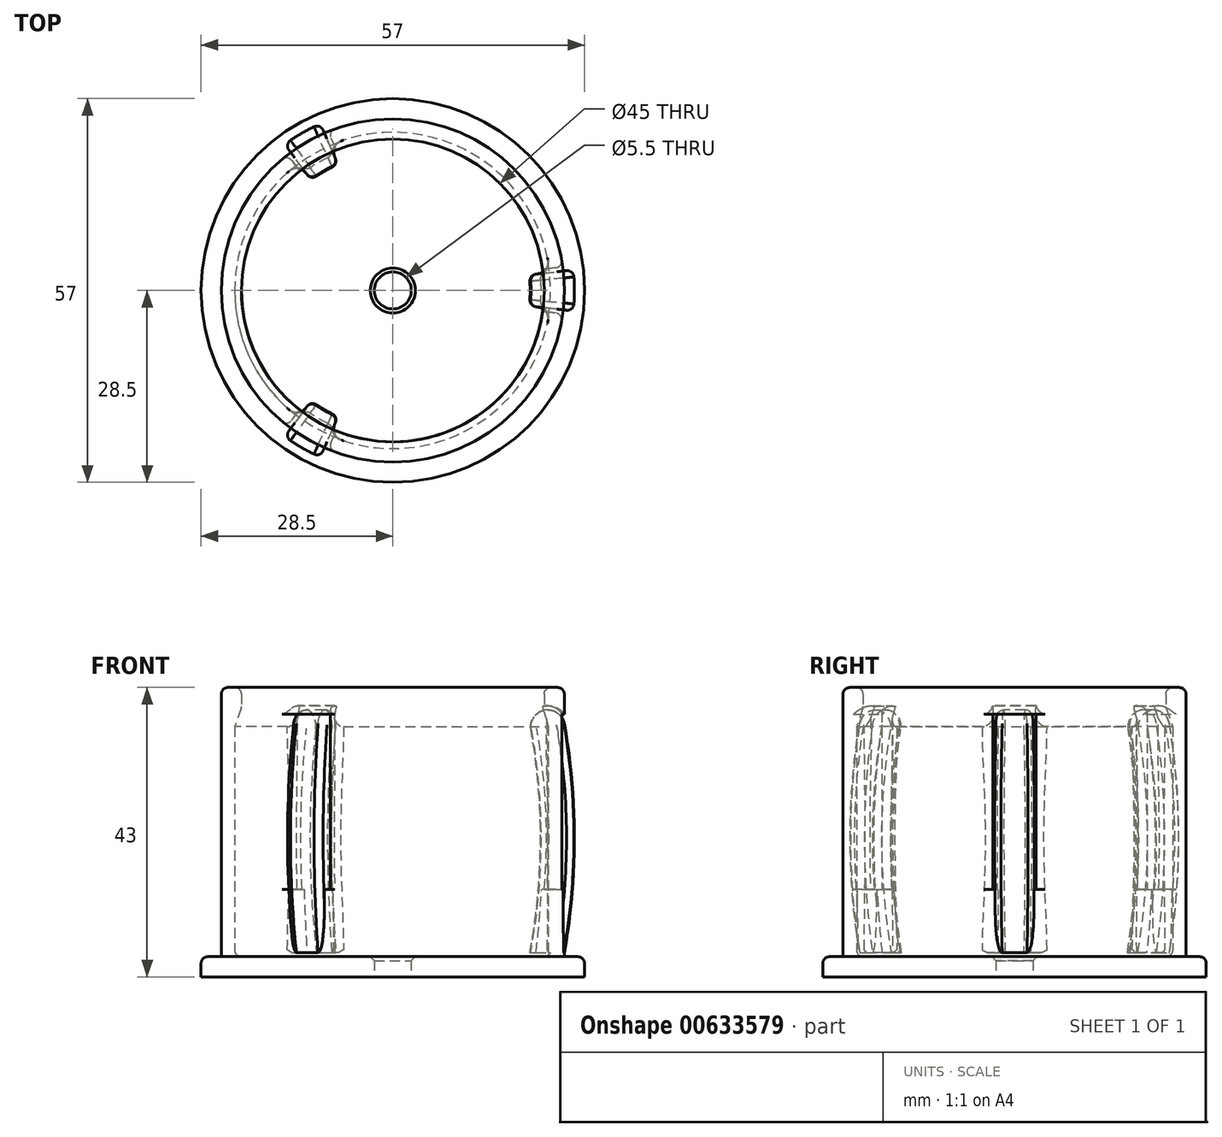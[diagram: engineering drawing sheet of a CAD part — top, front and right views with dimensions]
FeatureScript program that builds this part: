
annotation { "Feature Type Name" : "Feature", "Feature Type Description" : "" }
export const myFeature = defineFeature(function(context is Context, id is Id, definition is map)
    precondition{}
    {
        {
            var Q0;
            Q0=qCreatedBy(makeId("Front.planeOp"),FACE);
            var sketch = newSketch(context, id + "F0", { "sketchPlane" : qUnion([Q0])});
            skLineSegment(sketch, "E0", {"start": v(2.75, -1.5) * mm, "end": v(2.75, 1.5) * mm});
            skLineSegment(sketch, "E1", {"start": v(2.75, 1.5) * mm, "end": v(23.5, 1.5) * mm});
            skLineSegment(sketch, "E2", {"start": v(25.5, 1.5) * mm, "end": v(25.5, 41.5) * mm});
            skLineSegment(sketch, "E3", {"start": v(22.5, 41.5) * mm, "end": v(25.5, 41.5) * mm});
            skLineSegment(sketch, "E4", {"start": v(23.5, 35.67) * mm, "end": v(23.5, 1.5) * mm});
            skLineSegment(sketch, "E5", {"start": v(25.5, 1.5) * mm, "end": v(28.5, 1.5) * mm});
            skLineSegment(sketch, "E6", {"start": v(28.5, 1.5) * mm, "end": v(28.5, -1.5) * mm});
            skLineSegment(sketch, "E7", {"start": v(28.5, -1.5) * mm, "end": v(2.75, -1.5) * mm});
            skLineSegment(sketch, "E8", {"start": v(0, -12.71) * mm, "end": v(0, 50.95) * mm, "construction": true});
            skPoint(sketch, "E9.visualSharp", {"position": v(23.5, 1.5) * mm});
            skLineSegment(sketch, "E10", {"start": v(22.5, 41.5) * mm, "end": v(22.5, 38.5) * mm});
            skLineSegment(sketch, "E11", {"start": v(22.5, 38.5) * mm, "end": v(23.5, 35.67) * mm});
            skLineSegment(sketch, "E12", {"start": v(24.5, 1.5) * mm, "end": v(24.5, 41.5) * mm, "construction": true});
            skSolve(sketch);
        }
        {
            var Q0;
            Q0=qSketchRegion(id+"F0",true);
            var Q1;
            Q1=sQuery(id+"F0.wireOp",EDGE,"E8");
            revolve(context, id + "F1", {"entities" : qUnion([Q0]), "axis" : qUnion([Q1]), "revolveType" : RevolveType.FULL});
        }
        {
            var Q0;
            Q0=qCreatedBy(makeId("Front.planeOp"),FACE);
            var sketch = newSketch(context, id + "F2", { "sketchPlane" : qUnion([Q0])});
            skLineSegment(sketch, "E13", {"start": v(27, 29.31) * mm, "end": v(27, 4.9) * mm, "construction": true});
            skArc(sketch, "E14", {"start": v(25.5, 36.1) * mm, "mid": v(27, 19.1) * mm, "end": v(25.5, 2.1) * mm});
            skArc(sketch, "E15", {"start": v(20.58, 35.23) * mm, "mid": v(22, 18.66) * mm, "end": v(20.42, 2.1) * mm});
            skLineSegment(sketch, "E16", {"start": v(20.42, 2.1) * mm, "end": v(25.5, 2.1) * mm});
            skArc(sketch, "E17", {"start": v(20.58, 35.23) * mm, "mid": v(22.6, 38.13) * mm, "end": v(25.5, 36.1) * mm});
            skLineSegment(sketch, "E18", {"start": v(21.36, 35.67) * mm, "end": v(26.51, 35.67) * mm, "construction": true});
            skSolve(sketch);
        }
        {
            var Q0;
            Q0=qSketchRegion(id+"F2",true);
            var Q1;
            Q1=sQuery(id+"F0.wireOp",EDGE,"E8");
            revolve(context, id + "F3", {"entities" : qUnion([Q0]), "axis" : qUnion([Q1]), "revolveType" : RevolveType.SYMMETRIC, "angle" : 13 * degree});
        }
        {
            var Q0;
            Q0=makeQuery(id+"F3.opRevolve","SWEPT_BODY",BODY,{"disambiguationData":[OSD([sQuery(id+"F2.wireOp",EDGE,"E14"),sQuery(id+"F2.wireOp",EDGE,"E15"),sQuery(id+"F2.wireOp",EDGE,"ehrXcVqz-ctuI-yXWO-wcDy-QBcCehmGWMRg"),sQuery(id+"F2.wireOp",EDGE,"7emjYWeK-92yS-v46Q-MAfY-u0VWEbS8i3fu")])]});
            var Q1;
            Q1=sQuery(id+"F0.wireOp",EDGE,"E8");
            circularPattern(context, id + "F4", {"entities" : qUnion([Q0]), "axis" : qUnion([Q1]), "angle" : 360 * degree, "instanceCount" : 3, "equalSpace" : true});
        }
        {
            var Q0;
            Q0=makeQuery(id+"F3.opRevolve","SWEPT_BODY",BODY,{"disambiguationData":[OSD([sQuery(id+"F2.wireOp",EDGE,"E14"),sQuery(id+"F2.wireOp",EDGE,"E15"),sQuery(id+"F2.wireOp",EDGE,"ehrXcVqz-ctuI-yXWO-wcDy-QBcCehmGWMRg"),sQuery(id+"F2.wireOp",EDGE,"7emjYWeK-92yS-v46Q-MAfY-u0VWEbS8i3fu")])]});
            var Q1;
            Q1=makeQuery(id+"F4.opPattern","COPY",BODY,{"derivedFrom":makeQuery(id+"F3.opRevolve","SWEPT_BODY",BODY,{"disambiguationData":[OSD([sQuery(id+"F2.wireOp",EDGE,"E14"),sQuery(id+"F2.wireOp",EDGE,"E15"),sQuery(id+"F2.wireOp",EDGE,"ehrXcVqz-ctuI-yXWO-wcDy-QBcCehmGWMRg"),sQuery(id+"F2.wireOp",EDGE,"7emjYWeK-92yS-v46Q-MAfY-u0VWEbS8i3fu")])]}),"instanceName":"2"});
            var Q2;
            Q2=makeQuery(id+"F4.opPattern","COPY",BODY,{"derivedFrom":makeQuery(id+"F3.opRevolve","SWEPT_BODY",BODY,{"disambiguationData":[OSD([sQuery(id+"F2.wireOp",EDGE,"E14"),sQuery(id+"F2.wireOp",EDGE,"E15"),sQuery(id+"F2.wireOp",EDGE,"ehrXcVqz-ctuI-yXWO-wcDy-QBcCehmGWMRg"),sQuery(id+"F2.wireOp",EDGE,"7emjYWeK-92yS-v46Q-MAfY-u0VWEbS8i3fu")])]}),"instanceName":"1"});
            var Q3;
            Q3=makeQuery(id+"F1.opRevolve","SWEPT_BODY",BODY,{"disambiguationData":[OSD([sQuery(id+"F0.wireOp",EDGE,"E0"),sQuery(id+"F0.wireOp",EDGE,"E1"),sQuery(id+"F0.wireOp",EDGE,"E2"),sQuery(id+"F0.wireOp",EDGE,"E3"),sQuery(id+"F0.wireOp",EDGE,"E4"),sQuery(id+"F0.wireOp",EDGE,"E5"),sQuery(id+"F0.wireOp",EDGE,"E6"),sQuery(id+"F0.wireOp",EDGE,"E7")])]});
            booleanBodies(context, id + "F5", {"operationType" : BooleanOperationType.SUBTRACTION, "tools" : qUnion([Q0, Q1, Q2]), "targets" : qUnion([Q3]), "offset" : true, "offsetAll" : true, "offsetDistance" : 0.6 * mm, "reFillet" : true, "keepTools" : true});
        }
        {
            var Q0;
            Q0=makeQuery(id+"F1.opRevolve","SWEPT_FACE",FACE,{"disambiguationData":[OSD([sQuery(id+"F0.wireOp",EDGE,"E1")])]});
            var sketch = newSketch(context, id + "F6", { "sketchPlane" : qUnion([Q0])});
            skCircle(sketch, "E19", {"center": v(0, 0) * mm, "radius": 23.5 * mm});
            skCircle(sketch, "E20", {"center": v(0, 0) * mm, "radius": 25.5 * mm});
            skSolve(sketch);
        }
        {
            var Q0;
            Q0=qSketchRegion(id+"F6",true);
            extrude(context, id + "F7", {"entities" : qUnion([Q0]), "depth" : 10 * mm});
        }
        {
            var Q0;
            Q0=makeQuery(id+"F1.opRevolve","SWEPT_BODY",BODY,{"disambiguationData":[OSD([sQuery(id+"F0.wireOp",EDGE,"E0"),sQuery(id+"F0.wireOp",EDGE,"E1"),sQuery(id+"F0.wireOp",EDGE,"E2"),sQuery(id+"F0.wireOp",EDGE,"E3"),sQuery(id+"F0.wireOp",EDGE,"E4"),sQuery(id+"F0.wireOp",EDGE,"E5"),sQuery(id+"F0.wireOp",EDGE,"E6"),sQuery(id+"F0.wireOp",EDGE,"E7")])]});
            var Q1;
            Q1=makeQuery(id+"FhO7E1VeGoCWiRw_1.opExtrude","SWEPT_BODY",BODY,{"disambiguationData":[OSD([sQuery(id+"F2.wireOp",EDGE,"E14"),sQuery(id+"F2.wireOp",EDGE,"E15"),sQuery(id+"F2.wireOp",EDGE,"ehrXcVqz-ctuI-yXWO-wcDy-QBcCehmGWMRg"),sQuery(id+"F2.wireOp",EDGE,"7emjYWeK-92yS-v46Q-MAfY-u0VWEbS8i3fu")])]});
            var Q2;
            Q2=makeQuery(id+"F4.opPattern","COPY",BODY,{"derivedFrom":makeQuery(id+"FhO7E1VeGoCWiRw_1.opExtrude","SWEPT_BODY",BODY,{"disambiguationData":[OSD([sQuery(id+"F2.wireOp",EDGE,"E14"),sQuery(id+"F2.wireOp",EDGE,"E15"),sQuery(id+"F2.wireOp",EDGE,"ehrXcVqz-ctuI-yXWO-wcDy-QBcCehmGWMRg"),sQuery(id+"F2.wireOp",EDGE,"7emjYWeK-92yS-v46Q-MAfY-u0VWEbS8i3fu")])]}),"instanceName":"1"});
            var Q3;
            Q3=makeQuery(id+"F4.opPattern","COPY",BODY,{"derivedFrom":makeQuery(id+"FhO7E1VeGoCWiRw_1.opExtrude","SWEPT_BODY",BODY,{"disambiguationData":[OSD([sQuery(id+"F2.wireOp",EDGE,"E14"),sQuery(id+"F2.wireOp",EDGE,"E15"),sQuery(id+"F2.wireOp",EDGE,"ehrXcVqz-ctuI-yXWO-wcDy-QBcCehmGWMRg"),sQuery(id+"F2.wireOp",EDGE,"7emjYWeK-92yS-v46Q-MAfY-u0VWEbS8i3fu")])]}),"instanceName":"2"});
            var Q4;
            Q4=makeQuery(id+"F7.opExtrude","SWEPT_BODY",BODY,{"disambiguationData":[OSD([sQuery(id+"F6.wireOp",EDGE,"E19"),sQuery(id+"F6.wireOp",EDGE,"E20")])]});
            booleanBodies(context, id + "F8", {"operationType" : BooleanOperationType.UNION, "tools" : qUnion([Q0, Q1, Q2, Q3, Q4])});
        }
        {
            var Q0;
            Q0=makeQuery(id+"F1.opRevolve","SWEPT_BODY",BODY,{"disambiguationData":[OSD([sQuery(id+"F0.wireOp",EDGE,"E0"),sQuery(id+"F0.wireOp",EDGE,"E1"),sQuery(id+"F0.wireOp",EDGE,"E2"),sQuery(id+"F0.wireOp",EDGE,"E3"),sQuery(id+"F0.wireOp",EDGE,"E4"),sQuery(id+"F0.wireOp",EDGE,"E5"),sQuery(id+"F0.wireOp",EDGE,"E6"),sQuery(id+"F0.wireOp",EDGE,"E7")])]});
            var Q1;
            Q1=makeQuery(id+"F3.opRevolve","SWEPT_BODY",BODY,{"disambiguationData":[OSD([sQuery(id+"F2.wireOp",EDGE,"E14"),sQuery(id+"F2.wireOp",EDGE,"E15"),sQuery(id+"F2.wireOp",EDGE,"ehrXcVqz-ctuI-yXWO-wcDy-QBcCehmGWMRg"),sQuery(id+"F2.wireOp",EDGE,"7emjYWeK-92yS-v46Q-MAfY-u0VWEbS8i3fu")])]});
            var Q2;
            Q2=makeQuery(id+"F4.opPattern","COPY",BODY,{"derivedFrom":makeQuery(id+"F3.opRevolve","SWEPT_BODY",BODY,{"disambiguationData":[OSD([sQuery(id+"F2.wireOp",EDGE,"E14"),sQuery(id+"F2.wireOp",EDGE,"E15"),sQuery(id+"F2.wireOp",EDGE,"ehrXcVqz-ctuI-yXWO-wcDy-QBcCehmGWMRg"),sQuery(id+"F2.wireOp",EDGE,"7emjYWeK-92yS-v46Q-MAfY-u0VWEbS8i3fu")])]}),"instanceName":"1"});
            var Q3;
            Q3=makeQuery(id+"F4.opPattern","COPY",BODY,{"derivedFrom":makeQuery(id+"F3.opRevolve","SWEPT_BODY",BODY,{"disambiguationData":[OSD([sQuery(id+"F2.wireOp",EDGE,"E14"),sQuery(id+"F2.wireOp",EDGE,"E15"),sQuery(id+"F2.wireOp",EDGE,"ehrXcVqz-ctuI-yXWO-wcDy-QBcCehmGWMRg"),sQuery(id+"F2.wireOp",EDGE,"7emjYWeK-92yS-v46Q-MAfY-u0VWEbS8i3fu")])]}),"instanceName":"2"});
            booleanBodies(context, id + "F9", {"operationType" : BooleanOperationType.UNION, "tools" : qUnion([Q0, Q1, Q2, Q3])});
        }
        {
            var Q0;
            Q0=makeQuery(id+"F4.opPattern","COPY",EDGE,{"derivedFrom":makeQuery(id+"F3.opRevolve","CAP_EDGE",EDGE,{"disambiguationData":[OSD([sQuery(id+"F2.wireOp",EDGE,"E14")])],"isStart":false}),"instanceName":"1"});
            var Q1;
            Q1=makeQuery(id+"F4.opPattern","COPY",EDGE,{"derivedFrom":makeQuery(id+"F3.opRevolve","CAP_EDGE",EDGE,{"disambiguationData":[OSD([sQuery(id+"F2.wireOp",EDGE,"E14")])],"isStart":true}),"instanceName":"1"});
            var Q2;
            Q2=makeQuery(id+"F4.opPattern","COPY",EDGE,{"derivedFrom":makeQuery(id+"F3.opRevolve","CAP_EDGE",EDGE,{"disambiguationData":[OSD([sQuery(id+"F2.wireOp",EDGE,"E14")])],"isStart":true}),"instanceName":"2"});
            var Q3;
            Q3=makeQuery(id+"F4.opPattern","COPY",EDGE,{"derivedFrom":makeQuery(id+"F3.opRevolve","CAP_EDGE",EDGE,{"disambiguationData":[OSD([sQuery(id+"F2.wireOp",EDGE,"E14")])],"isStart":false}),"instanceName":"2"});
            var Q4;
            Q4=makeQuery(id+"F3.opRevolve","CAP_EDGE",EDGE,{"disambiguationData":[OSD([sQuery(id+"F2.wireOp",EDGE,"E14")])],"isStart":true});
            var Q5;
            Q5=makeQuery(id+"F3.opRevolve","CAP_EDGE",EDGE,{"disambiguationData":[OSD([sQuery(id+"F2.wireOp",EDGE,"E14")])],"isStart":false});
            var Q6;
            Q6=makeQuery(id+"F5.tempBoolean.opBoolean","INTERSECT",EDGE,{"derivedFrom":[makeQuery(id+"F1.opRevolve","SWEPT_FACE",FACE,{"disambiguationData":[OSD([sQuery(id+"F0.wireOp",EDGE,"E2")])]}),makeQuery(id+"F5.offsetTempBody.opPattern","COPY",FACE,{"derivedFrom":makeQuery(id+"F4.opPattern","COPY",FACE,{"derivedFrom":makeQuery(id+"F3.opRevolve","CAP_FACE",FACE,{"disambiguationData":[OSD([sQuery(id+"F2.wireOp",EDGE,"E14"),sQuery(id+"F2.wireOp",EDGE,"E15"),sQuery(id+"F2.wireOp",EDGE,"ehrXcVqz-ctuI-yXWO-wcDy-QBcCehmGWMRg"),sQuery(id+"F2.wireOp",EDGE,"7emjYWeK-92yS-v46Q-MAfY-u0VWEbS8i3fu")])],"isStart":false}),"instanceName":"1"}),"instanceName":"1"})]});
            var Q7;
            Q7=makeQuery(id+"F5.tempBoolean.opBoolean","INTERSECT",EDGE,{"derivedFrom":[makeQuery(id+"F1.opRevolve","SWEPT_FACE",FACE,{"disambiguationData":[OSD([sQuery(id+"F0.wireOp",EDGE,"E2")])]}),makeQuery(id+"F5.offsetTempBody.opPattern","COPY",FACE,{"derivedFrom":makeQuery(id+"F4.opPattern","COPY",FACE,{"derivedFrom":makeQuery(id+"F3.opRevolve","CAP_FACE",FACE,{"disambiguationData":[OSD([sQuery(id+"F2.wireOp",EDGE,"E14"),sQuery(id+"F2.wireOp",EDGE,"E15"),sQuery(id+"F2.wireOp",EDGE,"ehrXcVqz-ctuI-yXWO-wcDy-QBcCehmGWMRg"),sQuery(id+"F2.wireOp",EDGE,"7emjYWeK-92yS-v46Q-MAfY-u0VWEbS8i3fu")])],"isStart":true}),"instanceName":"1"}),"instanceName":"1"})]});
            var Q8;
            Q8=makeQuery(id+"F5.tempBoolean.opBoolean","INTERSECT",EDGE,{"derivedFrom":[makeQuery(id+"F1.opRevolve","SWEPT_FACE",FACE,{"disambiguationData":[OSD([sQuery(id+"F0.wireOp",EDGE,"E2")])]}),makeQuery(id+"F5.offsetTempBody.opPattern","COPY",FACE,{"derivedFrom":makeQuery(id+"F3.opRevolve","CAP_FACE",FACE,{"disambiguationData":[OSD([sQuery(id+"F2.wireOp",EDGE,"E14"),sQuery(id+"F2.wireOp",EDGE,"E15"),sQuery(id+"F2.wireOp",EDGE,"ehrXcVqz-ctuI-yXWO-wcDy-QBcCehmGWMRg"),sQuery(id+"F2.wireOp",EDGE,"7emjYWeK-92yS-v46Q-MAfY-u0VWEbS8i3fu")])],"isStart":false}),"instanceName":"1"})]});
            var Q9;
            Q9=makeQuery(id+"F5.tempBoolean.opBoolean","INTERSECT",EDGE,{"derivedFrom":[makeQuery(id+"F1.opRevolve","SWEPT_FACE",FACE,{"disambiguationData":[OSD([sQuery(id+"F0.wireOp",EDGE,"E2")])]}),makeQuery(id+"F5.offsetTempBody.opPattern","COPY",FACE,{"derivedFrom":makeQuery(id+"F3.opRevolve","CAP_FACE",FACE,{"disambiguationData":[OSD([sQuery(id+"F2.wireOp",EDGE,"E14"),sQuery(id+"F2.wireOp",EDGE,"E15"),sQuery(id+"F2.wireOp",EDGE,"ehrXcVqz-ctuI-yXWO-wcDy-QBcCehmGWMRg"),sQuery(id+"F2.wireOp",EDGE,"7emjYWeK-92yS-v46Q-MAfY-u0VWEbS8i3fu")])],"isStart":true}),"instanceName":"1"})]});
            var Q10;
            Q10=makeQuery(id+"F5.tempBoolean.opBoolean","INTERSECT",EDGE,{"derivedFrom":[makeQuery(id+"F1.opRevolve","SWEPT_FACE",FACE,{"disambiguationData":[OSD([sQuery(id+"F0.wireOp",EDGE,"E2")])]}),makeQuery(id+"F5.offsetTempBody.opPattern","COPY",FACE,{"derivedFrom":makeQuery(id+"F4.opPattern","COPY",FACE,{"derivedFrom":makeQuery(id+"F3.opRevolve","CAP_FACE",FACE,{"disambiguationData":[OSD([sQuery(id+"F2.wireOp",EDGE,"E14"),sQuery(id+"F2.wireOp",EDGE,"E15"),sQuery(id+"F2.wireOp",EDGE,"ehrXcVqz-ctuI-yXWO-wcDy-QBcCehmGWMRg"),sQuery(id+"F2.wireOp",EDGE,"7emjYWeK-92yS-v46Q-MAfY-u0VWEbS8i3fu")])],"isStart":false}),"instanceName":"2"}),"instanceName":"1"})]});
            var Q11;
            Q11=makeQuery(id+"F5.tempBoolean.opBoolean","INTERSECT",EDGE,{"derivedFrom":[makeQuery(id+"F1.opRevolve","SWEPT_FACE",FACE,{"disambiguationData":[OSD([sQuery(id+"F0.wireOp",EDGE,"E2")])]}),makeQuery(id+"F5.offsetTempBody.opPattern","COPY",FACE,{"derivedFrom":makeQuery(id+"F4.opPattern","COPY",FACE,{"derivedFrom":makeQuery(id+"F3.opRevolve","CAP_FACE",FACE,{"disambiguationData":[OSD([sQuery(id+"F2.wireOp",EDGE,"E14"),sQuery(id+"F2.wireOp",EDGE,"E15"),sQuery(id+"F2.wireOp",EDGE,"ehrXcVqz-ctuI-yXWO-wcDy-QBcCehmGWMRg"),sQuery(id+"F2.wireOp",EDGE,"7emjYWeK-92yS-v46Q-MAfY-u0VWEbS8i3fu")])],"isStart":true}),"instanceName":"2"}),"instanceName":"1"})]});
            var Q12;
            Q12=makeQuery(id+"F1.opRevolve","SWEPT_EDGE",EDGE,{"disambiguationData":[OSD([sQuery(id+"F0.wireOp",EDGE,"E5"),sQuery(id+"F0.wireOp",EDGE,"E6")])]});
            var Q13;
            Q13=makeQuery(id+"F1.opRevolve","SWEPT_EDGE",EDGE,{"disambiguationData":[OSD([sQuery(id+"F0.wireOp",EDGE,"E1"),sQuery(id+"F0.wireOp",EDGE,"E4")])]});
            var Q14;
            Q14=makeQuery(id+"F1.opRevolve","SWEPT_EDGE",EDGE,{"disambiguationData":[OSD([sQuery(id+"F0.wireOp",EDGE,"E2"),sQuery(id+"F0.wireOp",EDGE,"E3")])]});
            var Q15;
            Q15=makeQuery(id+"F1.opRevolve","SWEPT_EDGE",EDGE,{"disambiguationData":[OSD([sQuery(id+"F0.wireOp",EDGE,"E3"),sQuery(id+"F0.wireOp",EDGE,"E10")])]});
            var Q16;
            Q16=makeQuery(id+"F1.opRevolve","SWEPT_EDGE",EDGE,{"disambiguationData":[OSD([sQuery(id+"F0.wireOp",EDGE,"E10"),sQuery(id+"F0.wireOp",EDGE,"44e6730c-d766-4bbe-a9cf-efe5463532ff")])]});
            fillet(context, id + "F10", {"entities" : qUnion([Q0, Q1, Q2, Q3, Q4, Q5, Q6, Q7, Q8, Q9, Q10, Q11, Q12, Q13, Q14, Q15, Q16]), "radius" : 1 * mm, "tangentPropagation" : true, "allowEdgeOverflow" : false});
        }
        {
            var Q0;
            {var subQ2=sQuery(id+"F2.wireOp",EDGE,"E17");var subQ3=sQuery(id+"F2.wireOp",EDGE,"E16");var subQ4=sQuery(id+"F2.wireOp",EDGE,"E15");var subQ5=sQuery(id+"F2.wireOp",EDGE,"E14");var subQ6=makeQuery(id+"F3.opRevolve","CAP_FACE",FACE,{"disambiguationData":[OSD([subQ5,subQ4,subQ3,subQ2])],"isStart":false});var subQ7=makeQuery(id+"F3.opRevolve","CAP_FACE",FACE,{"disambiguationData":[OSD([subQ5,subQ4,subQ3,subQ2])],"isStart":true});var subQ8=makeQuery(id+"F1.opRevolve","SWEPT_FACE",FACE,{"disambiguationData":[OSD([sQuery(id+"F0.wireOp",EDGE,"E4")])]});Q0=makeQuery(id+"F9.opBoolean","INTERSECT",EDGE,{"derivedFrom":[subQ7,makeQuery(id+"F8.opBoolean","MERGE",FACE,{"derivedFrom":[makeQuery(id+"F5.tempBoolean.opBoolean","SPLIT",FACE,{"disambiguationData":[TD([makeQuery(id+"F5.offsetTempBody.opPattern","COPY",FACE,{"derivedFrom":subQ7,"instanceName":"1"})])],"derivedFrom":subQ8}),makeQuery(id+"F5.tempBoolean.opBoolean","SPLIT",FACE,{"disambiguationData":[TD([makeQuery(id+"F5.offsetTempBody.opPattern","COPY",FACE,{"derivedFrom":subQ6,"instanceName":"1"})])],"derivedFrom":subQ8}),makeQuery(id+"F5.tempBoolean.opBoolean","SPLIT",FACE,{"disambiguationData":[TD([makeQuery(id+"F5.offsetTempBody.opPattern","COPY",FACE,{"derivedFrom":makeQuery(id+"F4.opPattern","COPY",FACE,{"derivedFrom":subQ6,"instanceName":"1"}),"instanceName":"1"})])],"derivedFrom":subQ8}),makeQuery(id+"F7.opExtrude","SWEPT_FACE",FACE,{"disambiguationData":[OSD([sQuery(id+"F6.wireOp",EDGE,"E19")])]})]})]});}
            var Q1;
            {var subQ2=sQuery(id+"F2.wireOp",EDGE,"E17");var subQ3=sQuery(id+"F2.wireOp",EDGE,"E16");var subQ4=sQuery(id+"F2.wireOp",EDGE,"E15");var subQ5=sQuery(id+"F2.wireOp",EDGE,"E14");var subQ6=makeQuery(id+"F3.opRevolve","CAP_FACE",FACE,{"disambiguationData":[OSD([subQ5,subQ4,subQ3,subQ2])],"isStart":false});var subQ7=makeQuery(id+"F3.opRevolve","CAP_FACE",FACE,{"disambiguationData":[OSD([subQ5,subQ4,subQ3,subQ2])],"isStart":true});var subQ8=makeQuery(id+"F1.opRevolve","SWEPT_FACE",FACE,{"disambiguationData":[OSD([sQuery(id+"F0.wireOp",EDGE,"E4")])]});Q1=makeQuery(id+"F9.opBoolean","INTERSECT",EDGE,{"derivedFrom":[subQ6,makeQuery(id+"F8.opBoolean","MERGE",FACE,{"derivedFrom":[makeQuery(id+"F5.tempBoolean.opBoolean","SPLIT",FACE,{"disambiguationData":[TD([makeQuery(id+"F5.offsetTempBody.opPattern","COPY",FACE,{"derivedFrom":subQ7,"instanceName":"1"})])],"derivedFrom":subQ8}),makeQuery(id+"F5.tempBoolean.opBoolean","SPLIT",FACE,{"disambiguationData":[TD([makeQuery(id+"F5.offsetTempBody.opPattern","COPY",FACE,{"derivedFrom":subQ6,"instanceName":"1"})])],"derivedFrom":subQ8}),makeQuery(id+"F5.tempBoolean.opBoolean","SPLIT",FACE,{"disambiguationData":[TD([makeQuery(id+"F5.offsetTempBody.opPattern","COPY",FACE,{"derivedFrom":makeQuery(id+"F4.opPattern","COPY",FACE,{"derivedFrom":subQ6,"instanceName":"1"}),"instanceName":"1"})])],"derivedFrom":subQ8}),makeQuery(id+"F7.opExtrude","SWEPT_FACE",FACE,{"disambiguationData":[OSD([sQuery(id+"F6.wireOp",EDGE,"E19")])]})]})]});}
            var Q2;
            {var subQ2=sQuery(id+"F2.wireOp",EDGE,"E17");var subQ3=sQuery(id+"F2.wireOp",EDGE,"E16");var subQ4=sQuery(id+"F2.wireOp",EDGE,"E15");var subQ5=sQuery(id+"F2.wireOp",EDGE,"E14");var subQ6=makeQuery(id+"F3.opRevolve","CAP_FACE",FACE,{"disambiguationData":[OSD([subQ5,subQ4,subQ3,subQ2])],"isStart":false});var subQ7=makeQuery(id+"F3.opRevolve","CAP_FACE",FACE,{"disambiguationData":[OSD([subQ5,subQ4,subQ3,subQ2])],"isStart":true});var subQ8=makeQuery(id+"F1.opRevolve","SWEPT_FACE",FACE,{"disambiguationData":[OSD([sQuery(id+"F0.wireOp",EDGE,"E4")])]});var subQ9=makeQuery(id+"F4.opPattern","COPY",FACE,{"derivedFrom":subQ6,"instanceName":"2"});Q2=makeQuery(id+"F9.opBoolean","INTERSECT",EDGE,{"derivedFrom":[subQ9,makeQuery(id+"F8.opBoolean","MERGE",FACE,{"derivedFrom":[makeQuery(id+"F5.tempBoolean.opBoolean","SPLIT",FACE,{"disambiguationData":[TD([makeQuery(id+"F5.offsetTempBody.opPattern","COPY",FACE,{"derivedFrom":subQ7,"instanceName":"1"})])],"derivedFrom":subQ8}),makeQuery(id+"F5.tempBoolean.opBoolean","SPLIT",FACE,{"disambiguationData":[TD([makeQuery(id+"F5.offsetTempBody.opPattern","COPY",FACE,{"derivedFrom":subQ6,"instanceName":"1"})])],"derivedFrom":subQ8}),makeQuery(id+"F5.tempBoolean.opBoolean","SPLIT",FACE,{"disambiguationData":[TD([makeQuery(id+"F5.offsetTempBody.opPattern","COPY",FACE,{"derivedFrom":makeQuery(id+"F4.opPattern","COPY",FACE,{"derivedFrom":subQ6,"instanceName":"1"}),"instanceName":"1"})])],"derivedFrom":subQ8}),makeQuery(id+"F7.opExtrude","SWEPT_FACE",FACE,{"disambiguationData":[OSD([sQuery(id+"F6.wireOp",EDGE,"E19")])]})]})]});}
            var Q3;
            {var subQ2=sQuery(id+"F2.wireOp",EDGE,"E17");var subQ3=sQuery(id+"F2.wireOp",EDGE,"E16");var subQ4=sQuery(id+"F2.wireOp",EDGE,"E15");var subQ5=sQuery(id+"F2.wireOp",EDGE,"E14");var subQ6=makeQuery(id+"F3.opRevolve","CAP_FACE",FACE,{"disambiguationData":[OSD([subQ5,subQ4,subQ3,subQ2])],"isStart":false});var subQ7=makeQuery(id+"F3.opRevolve","CAP_FACE",FACE,{"disambiguationData":[OSD([subQ5,subQ4,subQ3,subQ2])],"isStart":true});var subQ8=makeQuery(id+"F4.opPattern","COPY",FACE,{"derivedFrom":subQ7,"instanceName":"2"});var subQ9=makeQuery(id+"F1.opRevolve","SWEPT_FACE",FACE,{"disambiguationData":[OSD([sQuery(id+"F0.wireOp",EDGE,"E4")])]});Q3=makeQuery(id+"F9.opBoolean","INTERSECT",EDGE,{"derivedFrom":[subQ8,makeQuery(id+"F8.opBoolean","MERGE",FACE,{"derivedFrom":[makeQuery(id+"F5.tempBoolean.opBoolean","SPLIT",FACE,{"disambiguationData":[TD([makeQuery(id+"F5.offsetTempBody.opPattern","COPY",FACE,{"derivedFrom":subQ7,"instanceName":"1"})])],"derivedFrom":subQ9}),makeQuery(id+"F5.tempBoolean.opBoolean","SPLIT",FACE,{"disambiguationData":[TD([makeQuery(id+"F5.offsetTempBody.opPattern","COPY",FACE,{"derivedFrom":subQ6,"instanceName":"1"})])],"derivedFrom":subQ9}),makeQuery(id+"F5.tempBoolean.opBoolean","SPLIT",FACE,{"disambiguationData":[TD([makeQuery(id+"F5.offsetTempBody.opPattern","COPY",FACE,{"derivedFrom":makeQuery(id+"F4.opPattern","COPY",FACE,{"derivedFrom":subQ6,"instanceName":"1"}),"instanceName":"1"})])],"derivedFrom":subQ9}),makeQuery(id+"F7.opExtrude","SWEPT_FACE",FACE,{"disambiguationData":[OSD([sQuery(id+"F6.wireOp",EDGE,"E19")])]})]})]});}
            var Q4;
            {var subQ2=sQuery(id+"F2.wireOp",EDGE,"E17");var subQ3=sQuery(id+"F2.wireOp",EDGE,"E16");var subQ4=sQuery(id+"F2.wireOp",EDGE,"E15");var subQ5=sQuery(id+"F2.wireOp",EDGE,"E14");var subQ6=makeQuery(id+"F3.opRevolve","CAP_FACE",FACE,{"disambiguationData":[OSD([subQ5,subQ4,subQ3,subQ2])],"isStart":false});var subQ7=makeQuery(id+"F4.opPattern","COPY",FACE,{"derivedFrom":subQ6,"instanceName":"1"});var subQ8=makeQuery(id+"F3.opRevolve","CAP_FACE",FACE,{"disambiguationData":[OSD([subQ5,subQ4,subQ3,subQ2])],"isStart":true});var subQ9=makeQuery(id+"F1.opRevolve","SWEPT_FACE",FACE,{"disambiguationData":[OSD([sQuery(id+"F0.wireOp",EDGE,"E4")])]});Q4=makeQuery(id+"F9.opBoolean","INTERSECT",EDGE,{"derivedFrom":[subQ7,makeQuery(id+"F8.opBoolean","MERGE",FACE,{"derivedFrom":[makeQuery(id+"F5.tempBoolean.opBoolean","SPLIT",FACE,{"disambiguationData":[TD([makeQuery(id+"F5.offsetTempBody.opPattern","COPY",FACE,{"derivedFrom":subQ8,"instanceName":"1"})])],"derivedFrom":subQ9}),makeQuery(id+"F5.tempBoolean.opBoolean","SPLIT",FACE,{"disambiguationData":[TD([makeQuery(id+"F5.offsetTempBody.opPattern","COPY",FACE,{"derivedFrom":subQ6,"instanceName":"1"})])],"derivedFrom":subQ9}),makeQuery(id+"F5.tempBoolean.opBoolean","SPLIT",FACE,{"disambiguationData":[TD([makeQuery(id+"F5.offsetTempBody.opPattern","COPY",FACE,{"derivedFrom":subQ7,"instanceName":"1"})])],"derivedFrom":subQ9}),makeQuery(id+"F7.opExtrude","SWEPT_FACE",FACE,{"disambiguationData":[OSD([sQuery(id+"F6.wireOp",EDGE,"E19")])]})]})]});}
            var Q5;
            {var subQ2=sQuery(id+"F2.wireOp",EDGE,"E17");var subQ3=sQuery(id+"F2.wireOp",EDGE,"E16");var subQ4=sQuery(id+"F2.wireOp",EDGE,"E15");var subQ5=sQuery(id+"F2.wireOp",EDGE,"E14");var subQ6=makeQuery(id+"F3.opRevolve","CAP_FACE",FACE,{"disambiguationData":[OSD([subQ5,subQ4,subQ3,subQ2])],"isStart":false});var subQ7=makeQuery(id+"F3.opRevolve","CAP_FACE",FACE,{"disambiguationData":[OSD([subQ5,subQ4,subQ3,subQ2])],"isStart":true});var subQ8=makeQuery(id+"F1.opRevolve","SWEPT_FACE",FACE,{"disambiguationData":[OSD([sQuery(id+"F0.wireOp",EDGE,"E4")])]});var subQ9=makeQuery(id+"F4.opPattern","COPY",FACE,{"derivedFrom":subQ7,"instanceName":"1"});Q5=makeQuery(id+"F9.opBoolean","INTERSECT",EDGE,{"derivedFrom":[subQ9,makeQuery(id+"F8.opBoolean","MERGE",FACE,{"derivedFrom":[makeQuery(id+"F5.tempBoolean.opBoolean","SPLIT",FACE,{"disambiguationData":[TD([makeQuery(id+"F5.offsetTempBody.opPattern","COPY",FACE,{"derivedFrom":subQ7,"instanceName":"1"})])],"derivedFrom":subQ8}),makeQuery(id+"F5.tempBoolean.opBoolean","SPLIT",FACE,{"disambiguationData":[TD([makeQuery(id+"F5.offsetTempBody.opPattern","COPY",FACE,{"derivedFrom":subQ6,"instanceName":"1"})])],"derivedFrom":subQ8}),makeQuery(id+"F5.tempBoolean.opBoolean","SPLIT",FACE,{"disambiguationData":[TD([makeQuery(id+"F5.offsetTempBody.opPattern","COPY",FACE,{"derivedFrom":makeQuery(id+"F4.opPattern","COPY",FACE,{"derivedFrom":subQ6,"instanceName":"1"}),"instanceName":"1"})])],"derivedFrom":subQ8}),makeQuery(id+"F7.opExtrude","SWEPT_FACE",FACE,{"disambiguationData":[OSD([sQuery(id+"F6.wireOp",EDGE,"E19")])]})]})]});}
            fillet(context, id + "F11", {"entities" : qUnion([Q0, Q1, Q2, Q3, Q4, Q5]), "radius" : 2 * mm, "rho" : 0.5, "crossSection" : FilletCrossSection.CONIC, "allowEdgeOverflow" : false});
        }
        {
            var Q0;
            {var subQ0=sQuery(id+"F2.wireOp",EDGE,"E16");var subQ3=sQuery(id+"F0.wireOp",EDGE,"E2");var subQ5=sQuery(id+"F0.wireOp",EDGE,"E5");var subQ8=sQuery(id+"F2.wireOp",EDGE,"E17");var subQ9=sQuery(id+"F2.wireOp",EDGE,"E15");var subQ10=sQuery(id+"F2.wireOp",EDGE,"E14");var subQ11=makeQuery(id+"F3.opRevolve","CAP_FACE",FACE,{"disambiguationData":[OSD([subQ10,subQ9,subQ0,subQ8])],"isStart":false});var subQ13=makeQuery(id+"F3.opRevolve","CAP_FACE",FACE,{"disambiguationData":[OSD([subQ10,subQ9,subQ0,subQ8])],"isStart":true});var subQ15=makeQuery(id+"F1.opRevolve","SWEPT_EDGE",EDGE,{"disambiguationData":[OSD([subQ3,subQ5])]});Q0=makeQuery(id+"F8.opBoolean","MERGE",EDGE,{"derivedFrom":[makeQuery(id+"F5.tempBoolean.opBoolean","SPLIT",EDGE,{"disambiguationData":[TD([makeQuery(id+"F5.offsetTempBody.opPattern","COPY",FACE,{"derivedFrom":subQ13,"instanceName":"1"})])],"derivedFrom":subQ15}),makeQuery(id+"F5.tempBoolean.opBoolean","SPLIT",EDGE,{"disambiguationData":[TD([makeQuery(id+"F5.offsetTempBody.opPattern","COPY",FACE,{"derivedFrom":subQ11,"instanceName":"1"})])],"derivedFrom":subQ15}),makeQuery(id+"F5.tempBoolean.opBoolean","SPLIT",EDGE,{"disambiguationData":[TD([makeQuery(id+"F5.offsetTempBody.opPattern","COPY",FACE,{"derivedFrom":makeQuery(id+"F4.opPattern","COPY",FACE,{"derivedFrom":subQ11,"instanceName":"1"}),"instanceName":"1"})])],"derivedFrom":subQ15}),makeQuery(id+"F7.opExtrude","CAP_EDGE",EDGE,{"disambiguationData":[OSD([sQuery(id+"F6.wireOp",EDGE,"E20")])],"isStart":true})]});}
            var Q1;
            Q1=makeQuery(id+"F1.opRevolve","SWEPT_EDGE",EDGE,{"disambiguationData":[OSD([sQuery(id+"F0.wireOp",EDGE,"E0"),sQuery(id+"F0.wireOp",EDGE,"E1")])]});
            chamfer(context, id + "F12", {"entities" : qUnion([Q0, Q1]), "width" : 0.6 * mm, "tangentPropagation" : true});
        }
    });
